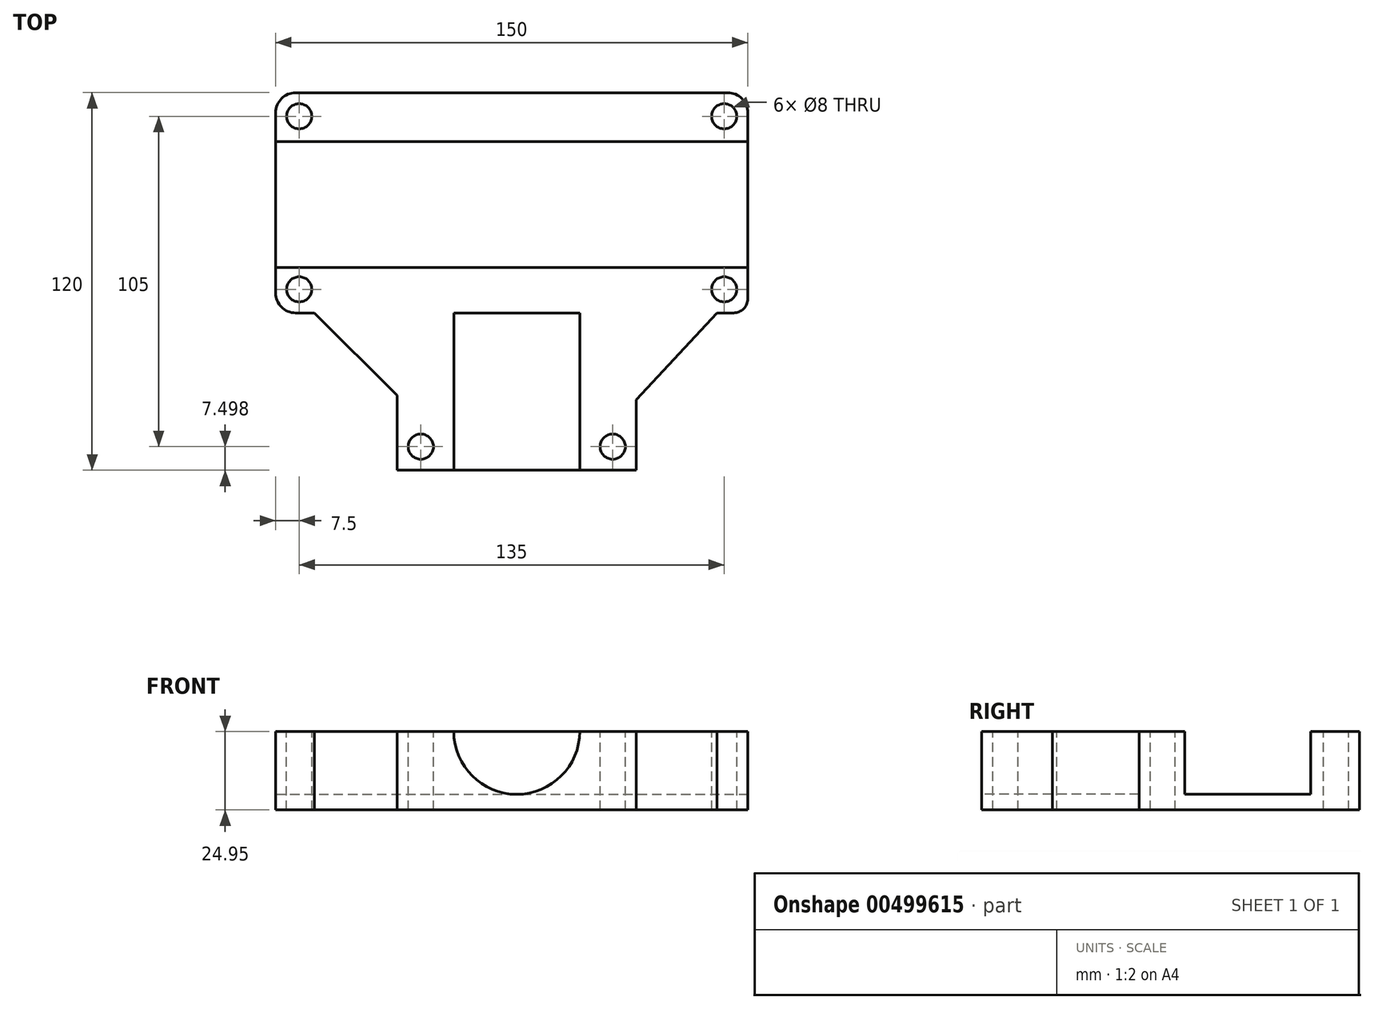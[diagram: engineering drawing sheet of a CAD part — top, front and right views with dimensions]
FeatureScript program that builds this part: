
annotation { "Feature Type Name" : "Feature", "Feature Type Description" : "" }
export const myFeature = defineFeature(function(context is Context, id is Id, definition is map)
    precondition{}
    {
        {
            var Q0;
            Q0=qCreatedBy(makeId("Top.planeOp"),FACE);
            var sketch = newSketch(context, id + "F0", { "sketchPlane" : qUnion([Q0])});
            skLineSegment(sketch, "E0.bottom", {"start": v(-78.94, 29.6) * mm, "end": v(58.18, 29.6) * mm});
            skLineSegment(sketch, "E0.top", {"start": v(-79.01, -40.4) * mm, "end": v(60.12, -40.4) * mm});
            skLineSegment(sketch, "E0.left", {"start": v(-85.38, 23.16) * mm, "end": v(-85.38, -34.03) * mm});
            skLineSegment(sketch, "E0.right", {"start": v(64.62, 23.16) * mm, "end": v(64.62, -35.9) * mm});
            skLineSegment(sketch, "E1.bottom", {"start": v(-43.28, -40.4) * mm, "end": v(26.72, -40.4) * mm});
            skArc(sketch, "E2.filletArc", {"start": v(-78.94, 29.6) * mm, "mid": v(-83.5, 27.71) * mm, "end": v(-85.38, 23.16) * mm});
            skPoint(sketch, "E3.visualSharp", {"position": v(64.62, 29.6) * mm});
            skArc(sketch, "E3.filletArc", {"start": v(64.62, 23.16) * mm, "mid": v(62.73, 27.71) * mm, "end": v(58.18, 29.6) * mm});
            skPoint(sketch, "E4.visualSharp", {"position": v(64.62, -40.4) * mm});
            skArc(sketch, "E4.filletArc", {"start": v(60.12, -40.4) * mm, "mid": v(63.3, -39.08) * mm, "end": v(64.62, -35.9) * mm});
            skArc(sketch, "E5.filletArc", {"start": v(-85.38, -34.03) * mm, "mid": v(-83.51, -38.54) * mm, "end": v(-79.01, -40.4) * mm});
            skLineSegment(sketch, "E6", {"start": v(-43.28, -40.4) * mm, "end": v(-58.5, -40.4) * mm});
            skLineSegment(sketch, "E7", {"start": v(-46.75, -40.4) * mm, "end": v(-46.75, -90.4) * mm});
            skLineSegment(sketch, "E8", {"start": v(-46.75, -90.4) * mm, "end": v(29.21, -90.4) * mm});
            skLineSegment(sketch, "E9", {"start": v(29.21, -90.4) * mm, "end": v(29.21, -40.4) * mm});
            skLineSegment(sketch, "E10", {"start": v(-46.75, -66.56) * mm, "end": v(-73.02, -40.4) * mm});
            skLineSegment(sketch, "E11", {"start": v(54.84, -40.4) * mm, "end": v(29.21, -67.97) * mm});
            skPoint(sketch, "E12.centerSnap0", {"position": v(-9.45, -40.4) * mm});
            skCircle(sketch, "E13", {"center": v(-77.88, 22.1) * mm, "radius": 4 * mm});
            skCircle(sketch, "E14", {"center": v(57.12, 22.1) * mm, "radius": 4 * mm});
            skCircle(sketch, "E15", {"center": v(-77.88, -32.9) * mm, "radius": 4 * mm});
            skCircle(sketch, "E16", {"center": v(57.12, -32.9) * mm, "radius": 4 * mm});
            skLineSegment(sketch, "E17.bottom", {"start": v(-46.75, -90.4) * mm, "end": v(-39.25, -90.4) * mm});
            skLineSegment(sketch, "E17.left", {"start": v(-46.75, -90.4) * mm, "end": v(-46.75, -82.9) * mm});
            skCircle(sketch, "E18", {"center": v(-39.25, -82.9) * mm, "radius": 4 * mm});
            skLineSegment(sketch, "E19.bottom", {"start": v(29.21, -90.4) * mm, "end": v(21.71, -90.4) * mm});
            skLineSegment(sketch, "E19.left", {"start": v(29.21, -90.4) * mm, "end": v(29.21, -82.9) * mm});
            skCircle(sketch, "E20", {"center": v(21.71, -82.9) * mm, "radius": 4 * mm});
            skSolve(sketch);
        }
        {
            var Q0;
            Q0 = qSketchRegion(id + "F0", true);
            extrude(context, id + "F1", {"entities" : qUnion([Q0]), "oppositeDirection" : true, "depth" : 24.95 * mm});
        }
        {
            var Q0;
            Q0=makeQuery(id+"F1.opExtrude","SWEPT_FACE",FACE,{"disambiguationData":[OSD([sQuery(id+"F0.wireOp",EDGE,"E0.right")])]});
            var sketch = newSketch(context, id + "F2", { "sketchPlane" : qUnion([Q0])});
            skLineSegment(sketch, "E21", {"start": v(-25.9, 0) * mm, "end": v(-25.9, -20) * mm});
            skLineSegment(sketch, "E22", {"start": v(-25.9, -20) * mm, "end": v(14.1, -20) * mm});
            skLineSegment(sketch, "E23", {"start": v(14.1, -20) * mm, "end": v(14.1, 0) * mm});
            skSolve(sketch);
        }
        {
            var Q0;
            Q0 = qSketchRegion(id + "F2", true);
            var Q1;
            {var subQ0=sQuery(id+"F2.wireOp",EDGE,"E21");Q1=makeQuery(id+"F2.imprint","IMPRINT",FACE,{"disambiguationData":[TD([[makeQuery(id+"F2.imprint","IMPRINT",EDGE,{"derivedFrom":subQ0}),1.0]])]});}
            extrude(context, id + "F3", {"entities" : qUnion([Q0, Q1]), "operationType" : NewBodyOperationType.REMOVE, "oppositeDirection" : true, "depth" : 150 * mm, "hasSecondDirection" : true, "secondDirectionOppositeDirection" : false, "secondDirectionDepth" : 150 * mm});
        }
        {
            var Q0;
            Q0=makeQuery(id+"F1.opExtrude","SWEPT_FACE",FACE,{"disambiguationData":[OSD([sQuery(id+"F0.wireOp",EDGE,"E8"),sQuery(id+"F0.wireOp",EDGE,"E17.bottom"),sQuery(id+"F0.wireOp",EDGE,"E19.bottom")])]});
            var sketch = newSketch(context, id + "F4", { "sketchPlane" : qUnion([Q0])});
            skCircle(sketch, "E24", {"center": v(-8.77, 0) * mm, "radius": 20 * mm});
            skSolve(sketch);
        }
        {
            var Q0;
            Q0 = qSketchRegion(id + "F4", true);
            extrude(context, id + "F5", {"entities" : qUnion([Q0]), "operationType" : NewBodyOperationType.REMOVE, "oppositeDirection" : true, "depth" : 50 * mm});
        }
    });
